# Revit family: LTC-6SQD-S
name_source: partatom
category: Lighting Fixtures
revit_build: Autodesk Revit 2017 (Build: 20160225_1515(x64)
units: mm (PartAtom-declared; Revit-internal decimal feet)

## family parameters
Cut with Voids When Loaded = No
Host = Face
Light Source = Yes
OmniClass Number = 23.80.70.11.14.11
OmniClass Title = Downlights
Part Type = Normal
Room Calculation Point = No
Round Connector Dimension = Use Diameter
Shared = Yes

## types (5) — shared parameters
Apparent Load = 52 VA
Ceiling Cutout = 6.25 "
Color Filter = 16777215
Connector Description = Lighting Connector
Cutout Radius = 3.13 "
Default Elevation = 48 "
Description = LITEISTRY™ 6inch Square Cylinder Downlight
Dimming Lamp Color Temperature Shift = <None>
Emit Shape Visible in Rendering = Yes
Emit from Rectangle Length = 7.59 "
Emit from Rectangle Width = 7.59 "
Frequency = 60 Hz
Glass = Hubbell - White Glass
Height = 14 "
Is 120V = Yes
Is 277V = No
Lamp = LED's
Load Classification = Lighting
Manufacturer = Prescolite
Model = LTC-6SQD
Photometric Notes = More IES files download on Photometric Web Link
Photometric Web File = LTC-6SQD-P-06L35K8MD-DM1-S-BL.ies
Product Documentation Link = https://hubbellcdn.com
Product Material = Paint - Hubbell - Carbon Black
Product Page URL = https://www.hubbell.com
Reflector Finish = Paint - Hubbell - Carbon Black
Tilt Angle = -90.00°
URL = https://www.hubbell.com
Voltage = 120 V
Wattage Comments = 8-25
Width = 7.59 "

## per-type parameters (varying)
| type | Canopy Height | Canopy width | Recessed | SRMD |
| LTC-6SQD-S | 0.25 " | 7.59 " | Yes | No |
| LTC-6SQD-SRMD | 0.25 " | 7.59 " | No | Yes |
| LTC-6SQD-SCC | 3 " | 7.75 " | No | No |
| LTC-6SQD-SPC | 3 " | 7.75 " | Yes | No |
| LTC-6SQD-SPCC | 4.5 " | 7.83 " | No | No |

## geometry (parser evidence)
native form markers: Blend x4, Sweep x2
no freeform markers — native parametric forms only
